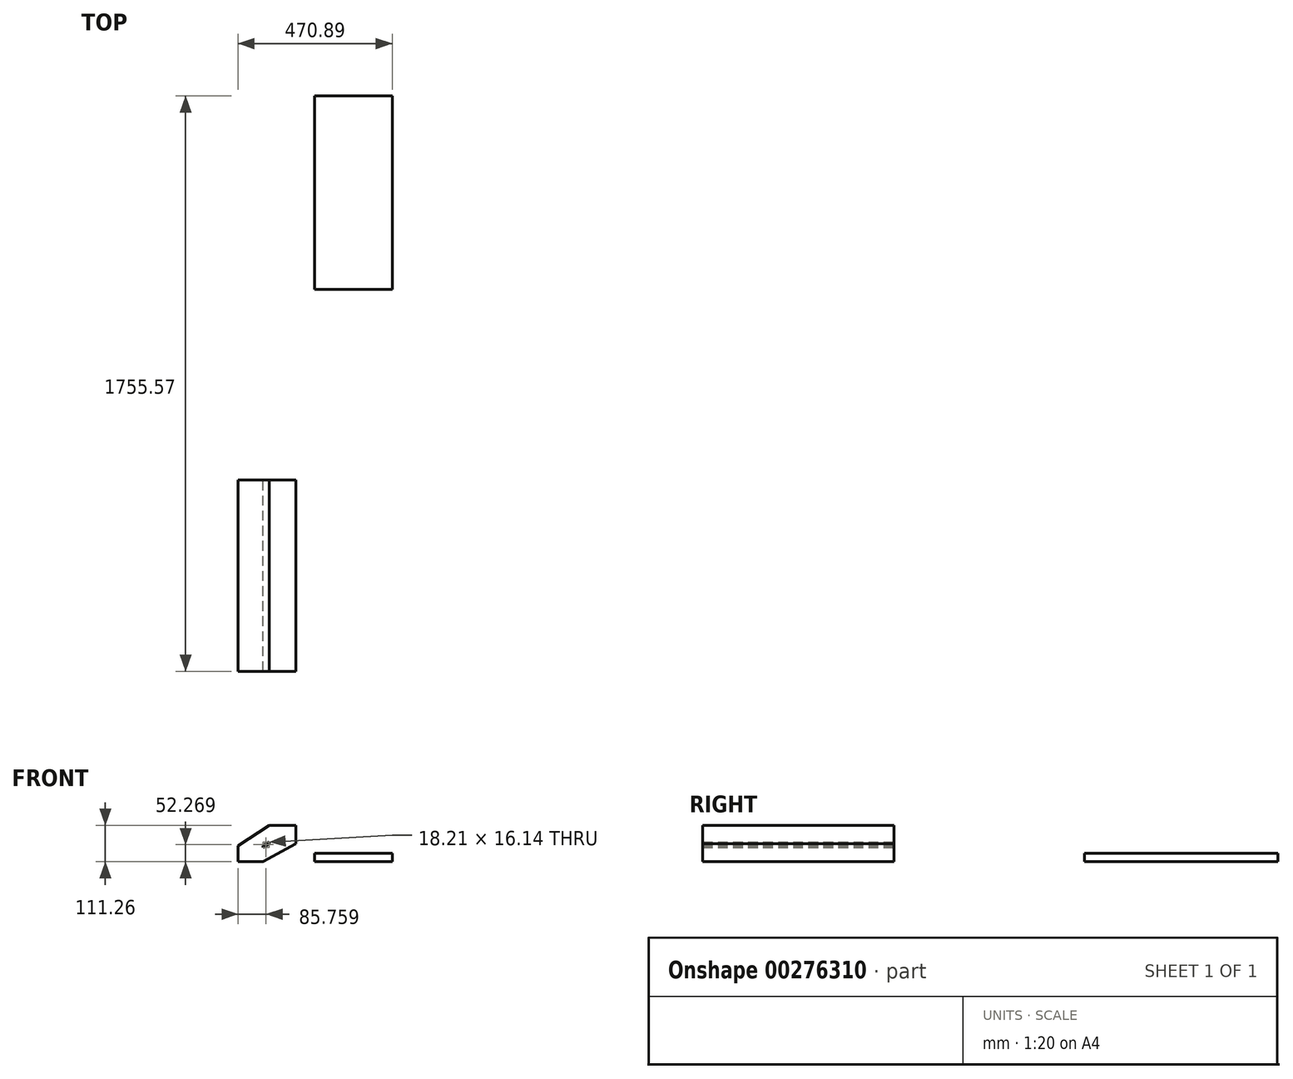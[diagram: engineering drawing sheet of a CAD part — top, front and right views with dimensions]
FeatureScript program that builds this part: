
annotation { "Feature Type Name" : "Feature", "Feature Type Description" : "" }
export const myFeature = defineFeature(function(context is Context, id is Id, definition is map)
    precondition{}
    {
        {
            var Q0;
            Q0=qCreatedBy(makeId("Front.planeOp"),FACE);
            var sketch = newSketch(context, id + "F0", { "sketchPlane" : qUnion([Q0])});
            skLineSegment(sketch, "E0.bottom", {"start": v(0, 0) * mm, "end": v(76.66, 0) * mm});
            skLineSegment(sketch, "E0.top", {"start": v(0, 48.96) * mm, "end": v(76.66, 48.96) * mm});
            skLineSegment(sketch, "E0.left", {"start": v(0, 0) * mm, "end": v(0, 48.96) * mm});
            skLineSegment(sketch, "E0.right", {"start": v(76.66, 0) * mm, "end": v(76.66, 48.96) * mm});
            skLineSegment(sketch, "E1.bottom", {"start": v(94.86, 54.7) * mm, "end": v(176.3, 54.7) * mm});
            skLineSegment(sketch, "E1.top", {"start": v(94.86, 111.26) * mm, "end": v(176.3, 111.26) * mm});
            skLineSegment(sketch, "E1.left", {"start": v(94.86, 54.7) * mm, "end": v(94.86, 111.26) * mm});
            skLineSegment(sketch, "E1.right", {"start": v(176.3, 54.7) * mm, "end": v(176.3, 111.26) * mm});
            skLineSegment(sketch, "E2", {"start": v(0, 48.96) * mm, "end": v(94.86, 111.26) * mm});
            skLineSegment(sketch, "E3", {"start": v(76.66, 48.96) * mm, "end": v(176.3, 111.26) * mm});
            skLineSegment(sketch, "E4", {"start": v(76.66, 0) * mm, "end": v(176.3, 54.7) * mm});
            skLineSegment(sketch, "E5", {"start": v(0, 0) * mm, "end": v(94.86, 54.7) * mm});
            skSolve(sketch);
        }
        {
            var Q0;
            Q0=qCreatedBy(makeId("Front.planeOp"),FACE);
            var sketch = newSketch(context, id + "F1", { "sketchPlane" : qUnion([Q0])});
            skLineSegment(sketch, "E6.bottom", {"start": v(-27.85, 0) * mm, "end": v(-75.46, 0) * mm});
            skLineSegment(sketch, "E6.top", {"start": v(-27.85, 75.1) * mm, "end": v(-75.46, 75.1) * mm});
            skLineSegment(sketch, "E6.left", {"start": v(-27.85, 0) * mm, "end": v(-27.85, 75.1) * mm});
            skLineSegment(sketch, "E6.right", {"start": v(-75.46, 0) * mm, "end": v(-75.46, 75.1) * mm});
            skSolve(sketch);
        }
        {
            var Q0;
            Q0=qCreatedBy(makeId("Top.planeOp"),FACE);
            var sketch = newSketch(context, id + "F2", { "sketchPlane" : qUnion([Q0])});
            skLineSegment(sketch, "E7.bottom", {"start": v(202.84, 473.7) * mm, "end": v(233.8, 473.7) * mm});
            skLineSegment(sketch, "E7.top", {"start": v(202.84, 580.85) * mm, "end": v(233.8, 580.85) * mm});
            skLineSegment(sketch, "E7.left", {"start": v(202.84, 473.7) * mm, "end": v(202.84, 580.85) * mm});
            skLineSegment(sketch, "E7.right", {"start": v(233.8, 473.7) * mm, "end": v(233.8, 580.85) * mm});
            skLineSegment(sketch, "E8.bottom", {"start": v(233.8, 580.85) * mm, "end": v(470.9, 580.85) * mm});
            skLineSegment(sketch, "E8.top", {"start": v(233.8, 1171.37) * mm, "end": v(470.9, 1171.37) * mm});
            skLineSegment(sketch, "E8.left", {"start": v(233.8, 580.85) * mm, "end": v(233.8, 1171.37) * mm});
            skLineSegment(sketch, "E8.right", {"start": v(470.9, 580.85) * mm, "end": v(470.9, 1171.37) * mm});
            skSolve(sketch);
        }
        {
            var Q0;
            Q0=makeQuery(id+"F2.imprint","IMPRINT",FACE,{"disambiguationData":[TD([[makeQuery(id+"F2.imprint","IMPRINT",EDGE,{"derivedFrom":sQuery(id+"F2.wireOp",EDGE,"E8.bottom")}),1.0]])]});
            extrude(context, id + "F3", {"entities" : qUnion([Q0]), "depth" : 25.4 * mm});
        }
        {
            var Q0;
            {var subQ0=sQuery(id+"F0.wireOp",EDGE,"E0.bottom");Q0=makeQuery(id+"F0.imprint","IMPRINT",FACE,{"disambiguationData":[TD([[makeQuery(id+"F0.imprint","IMPRINT",EDGE,{"derivedFrom":subQ0}),1.0]])]});}
            var Q1;
            {var subQ0=sQuery(id+"F0.wireOp",EDGE,"E0.top");Q1=makeQuery(id+"F0.imprint","IMPRINT",FACE,{"disambiguationData":[TD([[makeQuery(id+"F0.imprint","IMPRINT",EDGE,{"derivedFrom":subQ0}),1.0]])]});}
            var Q2;
            {var subQ0=sQuery(id+"F0.wireOp",EDGE,"E1.top");Q2=makeQuery(id+"F0.imprint","IMPRINT",FACE,{"disambiguationData":[TD([[makeQuery(id+"F0.imprint","IMPRINT",EDGE,{"derivedFrom":subQ0}),-1.0]])]});}
            var Q3;
            {var subQ0=sQuery(id+"F0.wireOp",EDGE,"E1.bottom");Q3=makeQuery(id+"F0.imprint","IMPRINT",FACE,{"disambiguationData":[TD([[makeQuery(id+"F0.imprint","IMPRINT",EDGE,{"derivedFrom":subQ0}),1.0]])]});}
            var Q4;
            {var subQ4=sQuery(id+"F0.wireOp",EDGE,"E1.bottom");Q4=makeQuery(id+"F0.imprint","IMPRINT",FACE,{"disambiguationData":[TD([[makeQuery(id+"F0.imprint","IMPRINT",EDGE,{"derivedFrom":subQ4}),-1.0]])]});}
            var Q5;
            {var subQ0=sQuery(id+"F0.wireOp",EDGE,"E0.top");Q5=makeQuery(id+"F0.imprint","IMPRINT",FACE,{"disambiguationData":[TD([[makeQuery(id+"F0.imprint","IMPRINT",EDGE,{"derivedFrom":subQ0}),-1.0]])]});}
            extrude(context, id + "F4", {"entities" : qUnion([Q0, Q1, Q2, Q3, Q4, Q5]), "depth" : 584.2 * mm});
        }
    });
